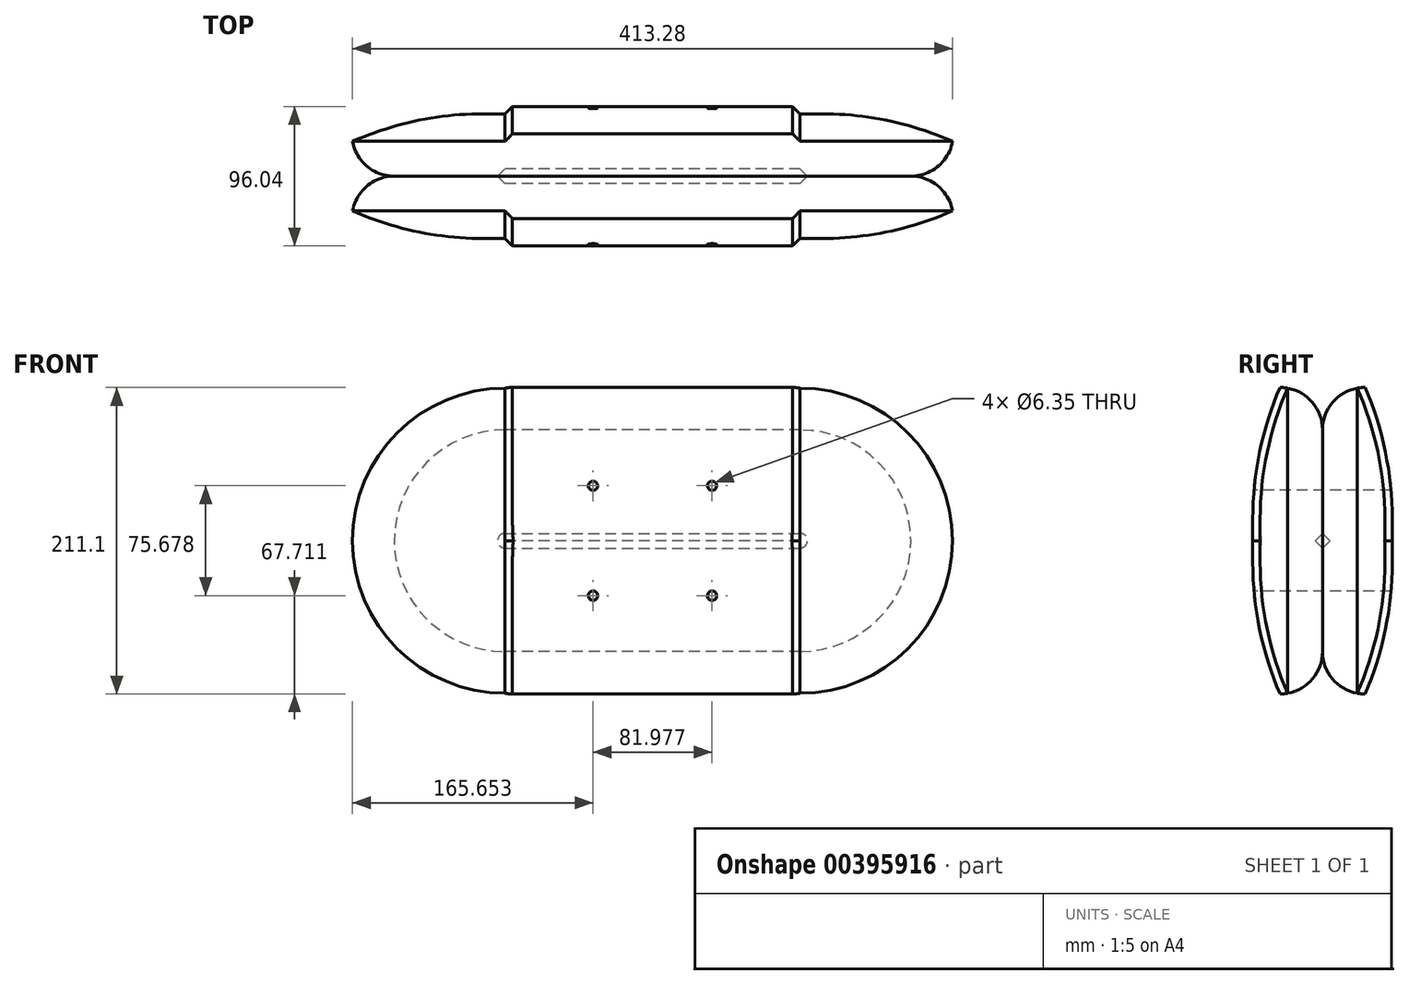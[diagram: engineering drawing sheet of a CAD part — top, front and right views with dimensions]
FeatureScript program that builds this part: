
annotation { "Feature Type Name" : "Feature", "Feature Type Description" : "" }
export const myFeature = defineFeature(function(context is Context, id is Id, definition is map)
    precondition{}
    {
        {
            var Q0;
            Q0=qCreatedBy(makeId("Top.planeOp"),FACE);
            var sketch = newSketch(context, id + "F0", { "sketchPlane" : qUnion([Q0])});
            skLineSegment(sketch, "E0.bottom", {"start": v(60.6, 0) * mm, "end": v(-40.99, 0) * mm});
            skLineSegment(sketch, "E0.top", {"start": v(60.6, 48.02) * mm, "end": v(-40.99, 48.02) * mm});
            skLineSegment(sketch, "E0.left", {"start": v(60.6, 0) * mm, "end": v(60.6, 48.02) * mm});
            skLineSegment(sketch, "E0.right", {"start": v(-40.99, 0) * mm, "end": v(-40.99, 48.02) * mm});
            skSolve(sketch);
        }
        {
            var Q0;
            Q0 = qSketchRegion(id + "F0", true);
            extrude(context, id + "F1", {"entities" : qUnion([Q0]), "depth" : 105.55 * mm});
        }
        {
            var Q0;
            Q0=makeQuery(id+"F1.opExtrude","CAP_EDGE",EDGE,{"disambiguationData":[OSD([sQuery(id+"F0.wireOp",EDGE,"E0.bottom")])],"isStart":false});
            fillet(context, id + "F2", {"entities" : qUnion([Q0]), "radius" : 29.25 * mm, "tangentPropagation" : true, "allowEdgeOverflow" : false});
        }
        {
            var Q0;
            Q0=makeQuery(id+"F1.opExtrude","CAP_EDGE",EDGE,{"disambiguationData":[OSD([sQuery(id+"F0.wireOp",EDGE,"E0.top")])],"isStart":false});
            fillet(context, id + "F3", {"entities" : qUnion([Q0]), "radius" : 227.73 * mm, "tangentPropagation" : true, "allowEdgeOverflow" : false});
        }
        {
            var Q0;
            Q0=makeQuery(id+"F1.opExtrude","CAP_EDGE",EDGE,{"disambiguationData":[OSD([sQuery(id+"F0.wireOp",EDGE,"E0.bottom")])],"isStart":true});
            chamfer(context, id + "F4", {"entities" : qUnion([Q0]), "width" : 5.08 * mm, "tangentPropagation" : true});
        }
        {
            var Q0;
            Q0=makeQuery(id+"F3.opFillet","BLEND_EDGE",EDGE,{"blendedFrom":[makeQuery(id+"F1.opExtrude","CAP_EDGE",EDGE,{"disambiguationData":[OSD([sQuery(id+"F0.wireOp",EDGE,"E0.top")])],"isStart":false}),makeQuery(id+"F1.opExtrude","SWEPT_FACE",FACE,{"disambiguationData":[OSD([sQuery(id+"F0.wireOp",EDGE,"E0.left")])]})],"blendedInto":[makeQuery(id+"F1.opExtrude","SWEPT_FACE",FACE,{"disambiguationData":[OSD([sQuery(id+"F0.wireOp",EDGE,"E0.left")])]})]});
            chamfer(context, id + "F5", {"entities" : qUnion([Q0]), "width" : 5.08 * mm});
        }
        {
            var Q0;
            Q0=qCreatedBy(makeId("Front.planeOp"),FACE);
            var sketch = newSketch(context, id + "F6", { "sketchPlane" : qUnion([Q0])});
            skPoint(sketch, "E1", {"position": v(0, 37.84) * mm});
            skSolve(sketch);
        }
        {
            var Q0;
            Q0=sQuery(id+"F6.wireOp",VERTEX,"E1");
            var Q1;
            Q1=makeQuery(id+"F1.opExtrude","SWEPT_BODY",BODY,{"disambiguationData":[OSD([sQuery(id+"F0.wireOp",EDGE,"E0.bottom"),sQuery(id+"F0.wireOp",EDGE,"E0.top"),sQuery(id+"F0.wireOp",EDGE,"E0.left"),sQuery(id+"F0.wireOp",EDGE,"E0.right")])]});
            hole(context, id + "F7", {"style" : HoleStyle.SIMPLE, "endStyle" : HoleEndStyle.THROUGH, "holeDiameter" : 6.35 * mm, "isTappedThrough" : true, "tappedDepth" : 12.7 * mm, "tapClearance" : 3, "locations" : qUnion([Q0]), "scope" : qUnion([Q1])});
        }
        {
            var Q0;
            Q0=makeQuery(id+"F1.opExtrude","SWEPT_BODY",BODY,{"disambiguationData":[OSD([sQuery(id+"F0.wireOp",EDGE,"E0.bottom"),sQuery(id+"F0.wireOp",EDGE,"E0.top"),sQuery(id+"F0.wireOp",EDGE,"E0.left"),sQuery(id+"F0.wireOp",EDGE,"E0.right")])]});
            var Q1;
            Q1=qCreatedBy(makeId("Front.planeOp"),FACE);
            mirror(context, id + "F8", {"operationType" : NewBodyOperationType.ADD, "entities" : qUnion([Q0]), "mirrorPlane" : qUnion([Q1])});
        }
        {
            var Q0;
            {var subQ0=makeQuery(id+"F1.opExtrude","SWEPT_FACE",FACE,{"disambiguationData":[OSD([sQuery(id+"F0.wireOp",EDGE,"E0.left")])]});Q0=makeQuery(id+"F8.boolean.opBoolean","MERGE",FACE,{"derivedFrom":[subQ0,makeQuery(id+"F8.opPattern","COPY",FACE,{"derivedFrom":subQ0,"instanceName":"1"})]});}
            var Q1;
            Q1=makeQuery(id+"F8.opPattern","COPY",EDGE,{"derivedFrom":makeQuery(id+"F1.opExtrude","CAP_EDGE",EDGE,{"disambiguationData":[OSD([sQuery(id+"F0.wireOp",EDGE,"E0.left")])],"isStart":true}),"instanceName":"1"});
            revolve(context, id + "F9", {"operationType" : NewBodyOperationType.ADD, "entities" : qUnion([Q0]), "axis" : qUnion([Q1]), "revolveType" : RevolveType.ONE_DIRECTION, "oppositeDirection" : true, "angle" : 180 * degree});
        }
        {
            var Q0;
            Q0=makeQuery(id+"F1.opExtrude","SWEPT_BODY",BODY,{"disambiguationData":[OSD([sQuery(id+"F0.wireOp",EDGE,"E0.bottom"),sQuery(id+"F0.wireOp",EDGE,"E0.top"),sQuery(id+"F0.wireOp",EDGE,"E0.left"),sQuery(id+"F0.wireOp",EDGE,"E0.right")])]});
            var Q1;
            Q1=makeQuery(id+"F1.opExtrude","CAP_FACE",FACE,{"disambiguationData":[OSD([sQuery(id+"F0.wireOp",EDGE,"E0.bottom"),sQuery(id+"F0.wireOp",EDGE,"E0.top"),sQuery(id+"F0.wireOp",EDGE,"E0.left"),sQuery(id+"F0.wireOp",EDGE,"E0.right")])],"isStart":true});
            mirror(context, id + "F10", {"operationType" : NewBodyOperationType.ADD, "entities" : qUnion([Q0]), "mirrorPlane" : qUnion([Q1])});
        }
        {
            var Q0;
            Q0=makeQuery(id+"F1.opExtrude","SWEPT_BODY",BODY,{"disambiguationData":[OSD([sQuery(id+"F0.wireOp",EDGE,"E0.bottom"),sQuery(id+"F0.wireOp",EDGE,"E0.top"),sQuery(id+"F0.wireOp",EDGE,"E0.left"),sQuery(id+"F0.wireOp",EDGE,"E0.right")])]});
            var Q1;
            {var subQ0=makeQuery(id+"F1.opExtrude","SWEPT_FACE",FACE,{"disambiguationData":[OSD([sQuery(id+"F0.wireOp",EDGE,"E0.right")])]});var subQ1=makeQuery(id+"F8.boolean.opBoolean","MERGE",FACE,{"derivedFrom":[subQ0,makeQuery(id+"F8.opPattern","COPY",FACE,{"derivedFrom":subQ0,"instanceName":"1"})]});Q1=makeQuery(id+"F10.boolean.opBoolean","MERGE",FACE,{"derivedFrom":[subQ1,makeQuery(id+"F10.opPattern","COPY",FACE,{"derivedFrom":subQ1,"instanceName":"1"})]});}
            mirror(context, id + "F11", {"operationType" : NewBodyOperationType.ADD, "entities" : qUnion([Q0]), "mirrorPlane" : qUnion([Q1])});
        }
    });
